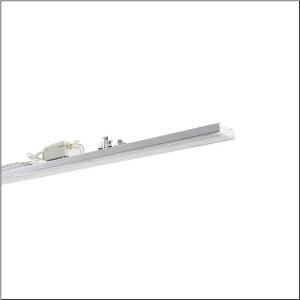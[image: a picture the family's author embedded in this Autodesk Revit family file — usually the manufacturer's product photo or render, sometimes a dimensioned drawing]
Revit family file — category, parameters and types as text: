
# Revit family: licross_r__21_recessed_mo_52te117n485g_1cb6
name_source: partatom
category: Lighting Fixtures
units: mm (PartAtom-declared; Revit-internal decimal feet)

## family parameters
Cut with Voids When Loaded = No
Host = Face
Light Source = No
Part Type = Normal
Room Calculation Point = No
Round Connector Dimension = Use Diameter
Shared = No

## types (1)
- Licross® 21 Recessed MO (1 x LED, 8680 lm, 47.9 W, 4000K)
    Apparent Load = 48 VA
    CIE Flux Codes = 89 96 99 100 100
    Color Rendering = 80
    Color Temperature = 4000K
    Default Elevation = 1800 mm
    Description = Licross® 21 Recessed MO, luminaire insert, of sheet steel, galvanised, coil coated, white, length: 1.500mm, width: 66mm, height: 67mm, LED rated luminous flux: 8.680lm, light colour: 840, control gear: ON/OFF, with plug, 3-pole, with phase selection, mains connection: 220..240V, AC, 50/60Hz, rated input power: 48W, halogen-free wiring, primary light control with lens, of plastic, primary optical cover: cover, of PMMA, light emission: direct distribution, primary light characteristic: symmetric, protection rating (complete): IP54, insulation class (complete): insulation class I (protective earthing), certification: CE, ENEC, VDE, UKCA, protection symbol: D if used in an environment with non-conductive dust loads with corresponding accessories, impact resistance: IK06, permissible ambient temperature for indoor applications: -35..+40°C, corresponds to IFS (International Featured Standards) requirements for safety and quality in the food industry, reducing of maximum allowable ambient temperature of 5°C with ceiling mounting, LABS conformity tested according to VDMA 24364:2018-05, packaging unit: 1 piece
    Height = 58 mm
    Lamp = 1 x LED
    Lamp Light Flux = 8680 lm
    Lamp Power = 47.9 W
    Lamp count = 1
    Length = 1500 mm
    Luminous efficacy = 181 lm/W
    Manufacturer = Siteco
    ModVariant = No
    Model = 52TE117N485G
    Mounting Place = Ceiling
    Mounting Type = Pendant
    Number of Poles = 1
    OnlyDefault = Yes
    Power Factor = 1
    Product Name = Licross® 21 Recessed MO
    Product group = luminaire insert
    ProductGroupID = 901
    Protection Class = Protection class I
    Protection Degree = IP 54
    RLX_Detail_Level = 1
    RLX_Emergency_Light_Flux = 0 lm
    RLX_Emergency_Type = 0
    RLX_Emergency_Type_DB = No
    RlxData = <blob elided: 20821 chars, md5=7c484433>
    Socket = socket
    Standby Power = 0 W
    System Light Flux = 8680 lm
    System Power = 48 W
    Type Comments = Product without accessories
    Type Image = l_1296930.jpg
    URL = http://relux.com
    VarID = ---
    Voltage = 0 V
    Weight = 0.00 kg
    Width = 66 mm

## geometry (parser evidence)
native form markers: Blend x4, Sweep x11
no freeform markers — native parametric forms only
